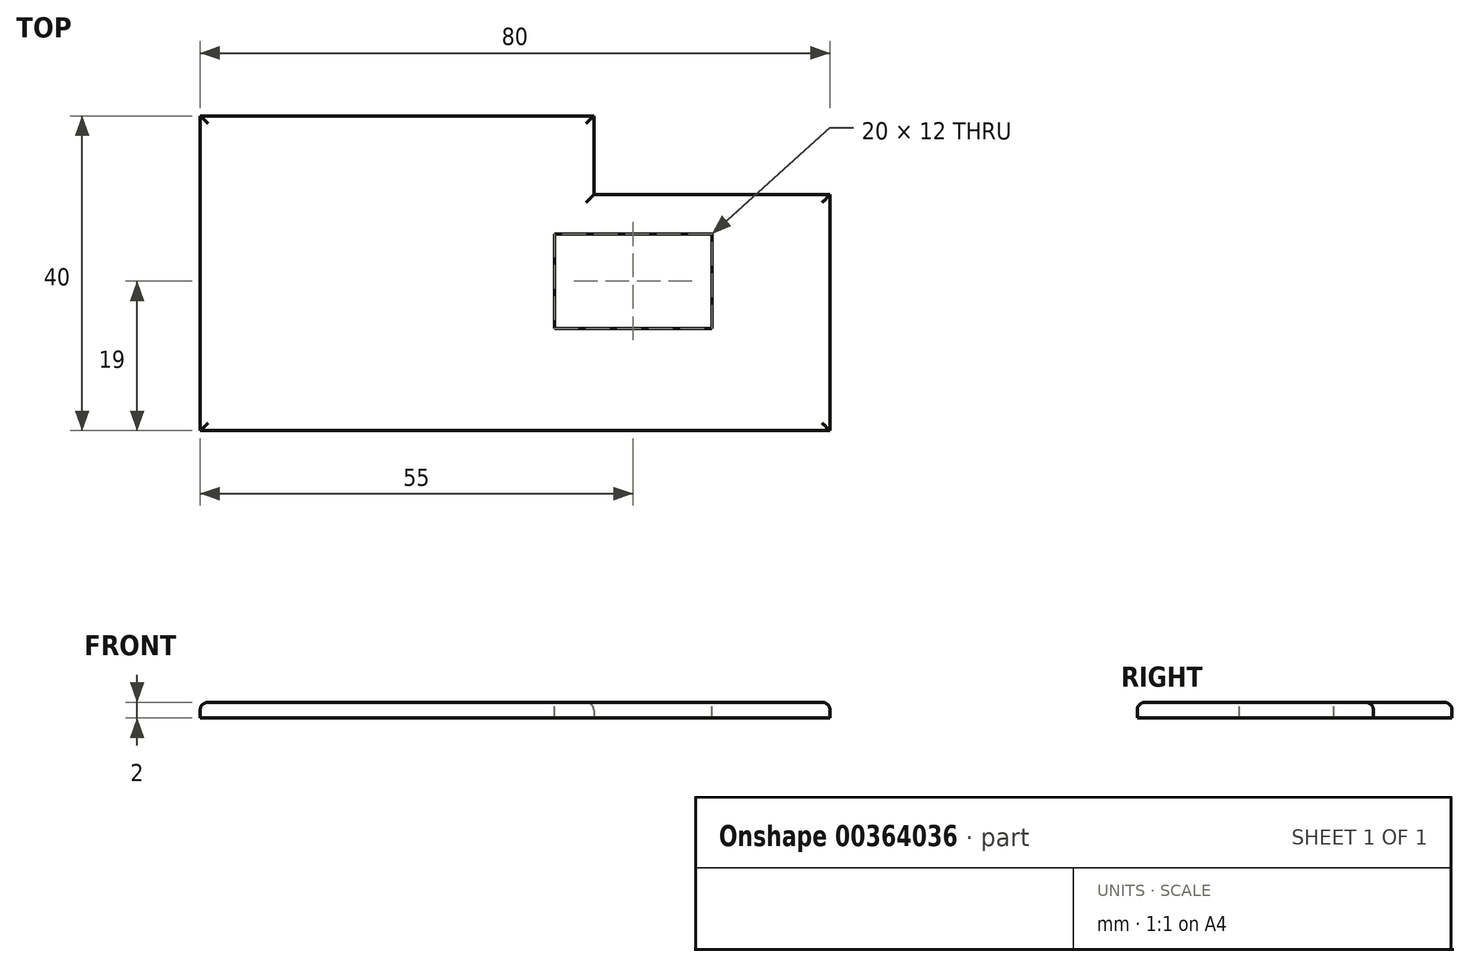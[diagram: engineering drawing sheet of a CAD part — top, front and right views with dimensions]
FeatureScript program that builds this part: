
annotation { "Feature Type Name" : "Feature", "Feature Type Description" : "" }
export const myFeature = defineFeature(function(context is Context, id is Id, definition is map)
    precondition{}
    {
        {
            var Q0;
            Q0=qCreatedBy(makeId("Top.planeOp"),FACE);
            var sketch = newSketch(context, id + "F0", { "sketchPlane" : qUnion([Q0])});
            skLineSegment(sketch, "E0", {"start": v(0, 0) * mm, "end": v(40, 0) * mm});
            skLineSegment(sketch, "E1", {"start": v(0, 0) * mm, "end": v(-40, 0) * mm});
            skLineSegment(sketch, "E2", {"start": v(-40, 0) * mm, "end": v(-40, 40) * mm});
            skLineSegment(sketch, "E3", {"start": v(-40, 40) * mm, "end": v(10, 40) * mm});
            skLineSegment(sketch, "E4", {"start": v(10, 40) * mm, "end": v(10, 30) * mm});
            skLineSegment(sketch, "E5", {"start": v(10, 30) * mm, "end": v(40, 30) * mm});
            skLineSegment(sketch, "E6", {"start": v(40, 30) * mm, "end": v(40, 0) * mm});
            skSolve(sketch);
        }
        {
            var Q0;
            Q0=makeQuery(id+"F0.imprint","IMPRINT",FACE,{"disambiguationData":[TD([[makeQuery(id+"F0.imprint","IMPRINT",EDGE,{"derivedFrom":sQuery(id+"F0.wireOp",EDGE,"E0")}),1.0]])]});
            extrude(context, id + "F1", {"entities" : qUnion([Q0]), "depth" : 2 * mm});
        }
        {
            var Q0;
            Q0=makeQuery(id+"F1.opExtrude","CAP_FACE",FACE,{"disambiguationData":[OSD([sQuery(id+"F0.wireOp",EDGE,"E0"),sQuery(id+"F0.wireOp",EDGE,"E1"),sQuery(id+"F0.wireOp",EDGE,"E2"),sQuery(id+"F0.wireOp",EDGE,"E3"),sQuery(id+"F0.wireOp",EDGE,"E4"),sQuery(id+"F0.wireOp",EDGE,"E5"),sQuery(id+"F0.wireOp",EDGE,"E6")])],"isStart":false});
            var sketch = newSketch(context, id + "F2", { "sketchPlane" : qUnion([Q0])});
            skLineSegment(sketch, "E7", {"start": v(-40, 40) * mm, "end": v(5, 40) * mm});
            skLineSegment(sketch, "E8", {"start": v(5, 25) * mm, "end": v(5, 13) * mm});
            skLineSegment(sketch, "E9", {"start": v(5, 13) * mm, "end": v(25, 13) * mm});
            skLineSegment(sketch, "E10", {"start": v(25, 13) * mm, "end": v(25, 25) * mm});
            skPoint(sketch, "E10.endSnap0", {"position": v(25, 30) * mm});
            skLineSegment(sketch, "E11", {"start": v(25, 25) * mm, "end": v(5, 25) * mm});
            skSolve(sketch);
        }
        {
            var Q0;
            Q0=makeQuery(id+"F2.imprint","IMPRINT",FACE,{"disambiguationData":[TD([[makeQuery(id+"F2.imprint","IMPRINT",EDGE,{"derivedFrom":sQuery(id+"F2.wireOp",EDGE,"E8")}),1.0]])]});
            extrude(context, id + "F3", {"entities" : qUnion([Q0]), "operationType" : NewBodyOperationType.REMOVE, "oppositeDirection" : true, "depth" : 5 * mm});
        }
        {
            var Q0;
            Q0=makeQuery(id+"F1.opExtrude","CAP_EDGE",EDGE,{"disambiguationData":[OSD([sQuery(id+"F0.wireOp",EDGE,"E3")])],"isStart":false});
            var Q1;
            Q1=makeQuery(id+"F1.opExtrude","CAP_EDGE",EDGE,{"disambiguationData":[OSD([sQuery(id+"F0.wireOp",EDGE,"E2")])],"isStart":false});
            var Q2;
            Q2=makeQuery(id+"F1.opExtrude","CAP_EDGE",EDGE,{"disambiguationData":[OSD([sQuery(id+"F0.wireOp",EDGE,"E0"),sQuery(id+"F0.wireOp",EDGE,"E1")])],"isStart":false});
            var Q3;
            Q3=makeQuery(id+"F1.opExtrude","CAP_EDGE",EDGE,{"disambiguationData":[OSD([sQuery(id+"F0.wireOp",EDGE,"E6")])],"isStart":false});
            var Q4;
            Q4=makeQuery(id+"F1.opExtrude","CAP_EDGE",EDGE,{"disambiguationData":[OSD([sQuery(id+"F0.wireOp",EDGE,"E5")])],"isStart":false});
            var Q5;
            Q5=makeQuery(id+"F1.opExtrude","CAP_EDGE",EDGE,{"disambiguationData":[OSD([sQuery(id+"F0.wireOp",EDGE,"E4")])],"isStart":false});
            var Q6;
            Q6=makeQuery(id+"F3.boolean.opBoolean","COPY",EDGE,{"derivedFrom":makeQuery(id+"F3.opExtrude","CAP_EDGE",EDGE,{"disambiguationData":[OSD([sQuery(id+"F2.wireOp",EDGE,"E11")])],"isStart":true})});
            var Q7;
            Q7=makeQuery(id+"F3.boolean.opBoolean","COPY",EDGE,{"derivedFrom":makeQuery(id+"F3.opExtrude","CAP_EDGE",EDGE,{"disambiguationData":[OSD([sQuery(id+"F2.wireOp",EDGE,"E8")])],"isStart":true})});
            var Q8;
            Q8=makeQuery(id+"F3.boolean.opBoolean","COPY",EDGE,{"derivedFrom":makeQuery(id+"F3.opExtrude","CAP_EDGE",EDGE,{"disambiguationData":[OSD([sQuery(id+"F2.wireOp",EDGE,"E9")])],"isStart":true})});
            var Q9;
            Q9=makeQuery(id+"F3.boolean.opBoolean","COPY",EDGE,{"derivedFrom":makeQuery(id+"F3.opExtrude","CAP_EDGE",EDGE,{"disambiguationData":[OSD([sQuery(id+"F2.wireOp",EDGE,"E10")])],"isStart":true})});
            fillet(context, id + "F4", {"entities" : qUnion([Q0, Q1, Q2, Q3, Q4, Q5, Q6, Q7, Q8, Q9]), "radius" : 1 * mm, "tangentPropagation" : true, "allowEdgeOverflow" : false});
        }
    });
